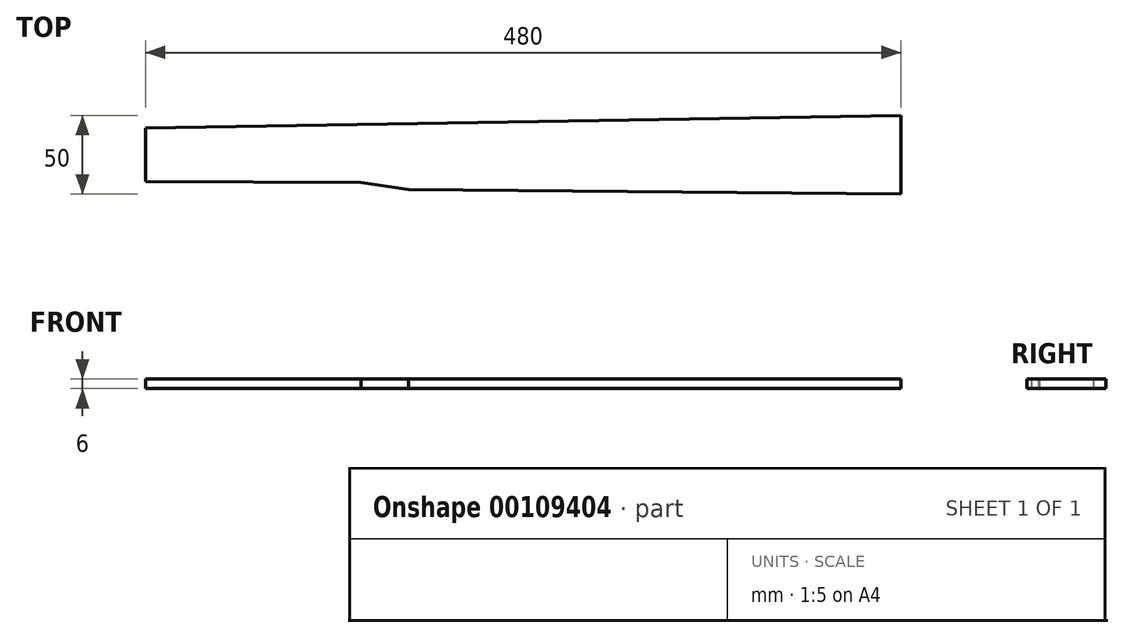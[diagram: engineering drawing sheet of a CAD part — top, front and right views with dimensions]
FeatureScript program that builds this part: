
annotation { "Feature Type Name" : "Feature", "Feature Type Description" : "" }
export const myFeature = defineFeature(function(context is Context, id is Id, definition is map)
    precondition{}
    {
        {
            var Q0;
            Q0=qCreatedBy(makeId("Top.planeOp"),FACE);
            var sketch = newSketch(context, id + "F0", { "sketchPlane" : qUnion([Q0])});
            skLineSegment(sketch, "E0", {"start": v(0, 0) * mm, "end": v(0, 17) * mm});
            skLineSegment(sketch, "E1", {"start": v(0, 0) * mm, "end": v(0, -17) * mm});
            skLineSegment(sketch, "E2", {"start": v(480, 16) * mm, "end": v(480, 25) * mm});
            skLineSegment(sketch, "E3", {"start": v(0, 0) * mm, "end": v(542, 0) * mm, "construction": true});
            skLineSegment(sketch, "E4", {"start": v(480, 25) * mm, "end": v(480, 0) * mm});
            skLineSegment(sketch, "E5", {"start": v(0, 17) * mm, "end": v(480, 25) * mm});
            skLineSegment(sketch, "E6", {"start": v(480, 0) * mm, "end": v(480, -25) * mm});
            skPoint(sketch, "E7", {"position": v(0, 13.5) * mm});
            skPoint(sketch, "E8", {"position": v(0, 4.5) * mm});
            skPoint(sketch, "E9", {"position": v(0, -4.5) * mm});
            skPoint(sketch, "E10", {"position": v(0, -13.5) * mm});
            skPoint(sketch, "E11", {"position": v(167, -22.22) * mm});
            skLineSegment(sketch, "E12", {"start": v(137, 46.94) * mm, "end": v(137, -62.1) * mm, "construction": true});
            skPoint(sketch, "E13", {"position": v(137, 19.28) * mm});
            skPoint(sketch, "E14", {"position": v(137, -17.72) * mm});
            skLineSegment(sketch, "E15", {"start": v(137, -17.72) * mm, "end": v(0, -17) * mm});
            skLineSegment(sketch, "E16", {"start": v(0, -4.5) * mm, "end": v(480, 0) * mm, "construction": true});
            skLineSegment(sketch, "E17", {"start": v(167, -22.22) * mm, "end": v(167, 19.78) * mm, "construction": true});
            skLineSegment(sketch, "E18", {"start": v(167, -22.22) * mm, "end": v(480, -25) * mm});
            skLineSegment(sketch, "E19", {"start": v(167, -22.22) * mm, "end": v(137, -17.72) * mm});
            skSolve(sketch);
        }
        {
            var Q0;
            Q0 = qSketchRegion(id + "F0", true);
            extrude(context, id + "F1", {"entities" : qUnion([Q0]), "depth" : 6 * mm});
        }
    });
